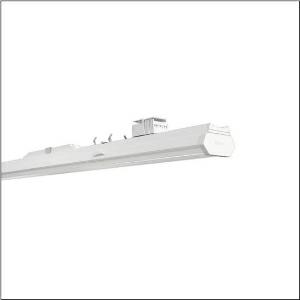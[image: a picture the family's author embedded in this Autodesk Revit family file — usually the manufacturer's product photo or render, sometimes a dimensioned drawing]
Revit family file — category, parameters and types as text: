
# Revit family: licross_r__21_performance_mo_52td167n445g_3390
name_source: partatom
category: Lighting Fixtures
units: mm (PartAtom-declared; Revit-internal decimal feet)

## family parameters
Cut with Voids When Loaded = No
Host = Face
Light Source = No
Part Type = Normal
Room Calculation Point = No
Round Connector Dimension = Use Diameter
Shared = No

## types (1)
- Licross® 21 Performance MO (1 x LED, 4580 lm, 24.7 W, 4000K)
    Apparent Load = 25 VA
    CIE Flux Codes = 66 88 96 79 100
    Color Rendering = 80
    Color Temperature = 4000K
    Default Elevation = 1800 mm
    Description = Licross® 21 Performance MO, luminaire insert, of sheet steel, galvanised, coil coated, white, length: 1.500mm, width: 120mm, height: 123mm, LED rated luminous flux: 4.580lm, light colour: 840, control gear: ON/OFF, control gear: ECG, with plug, 3-pole, with phase selection, mains connection: 220..240V, AC, 50/60Hz, halogen-free wiring, primary light control with lens, of plastic, primary optical cover: cover, of PMMA, CAT 2 (L<= 3000cd/m²), light emission: direct/indirect distribution, primary light characteristic: symmetric, protection rating (complete): IP54, insulation class (complete): insulation class I (protective earthing), certification: CE, ENEC, UKCA, protection symbol: D if used in an environment with non-conductive dust loads with corresponding accessories, impact resistance: IK06, permissible ambient temperature for indoor applications: -35..+55°C, corresponds to IFS (International Featured Standards) requirements for safety and quality in the food industry, reducing of maximum allowable ambient temperature of 5°C with ceiling mounting, LABS conformity tested according to VDMA 24364:2018-05, packaging unit: 1 piece
    Height = 114 mm
    Lamp = 1 x LED
    Lamp Light Flux = 4580 lm
    Lamp Power = 24.7 W
    Lamp count = 1
    Length = 1500 mm
    Luminous efficacy = 185 lm/W
    Manufacturer = Siteco
    ModVariant = No
    Model = 52TD167N445G
    Mounting Place = Ceiling
    Mounting Type = Pendant
    Number of Poles = 1
    OnlyDefault = Yes
    Power Factor = 1
    Product Name = Licross® 21 Performance MO
    Product group = luminaire insert
    ProductGroupID = 902
    Protection Class = Protection class I
    Protection Degree = IP 54
    RLX_Detail_Level = 1
    RlxData = <blob elided: 28317 chars, md5=f2a8d3ce>
    Socket = socket
    Standby Power = 0 W
    System Light Flux = 4580 lm
    System Power = 25 W
    Type Comments = Product without accessories
    Type Image = l_1256148.jpg
    URL = http://relux.com
    VarID = ---
    Voltage = 0 V
    Weight = 0.00 kg
    Width = 120 mm

## geometry (parser evidence)
native form markers: Blend x4, Sweep x12
no freeform markers — native parametric forms only
